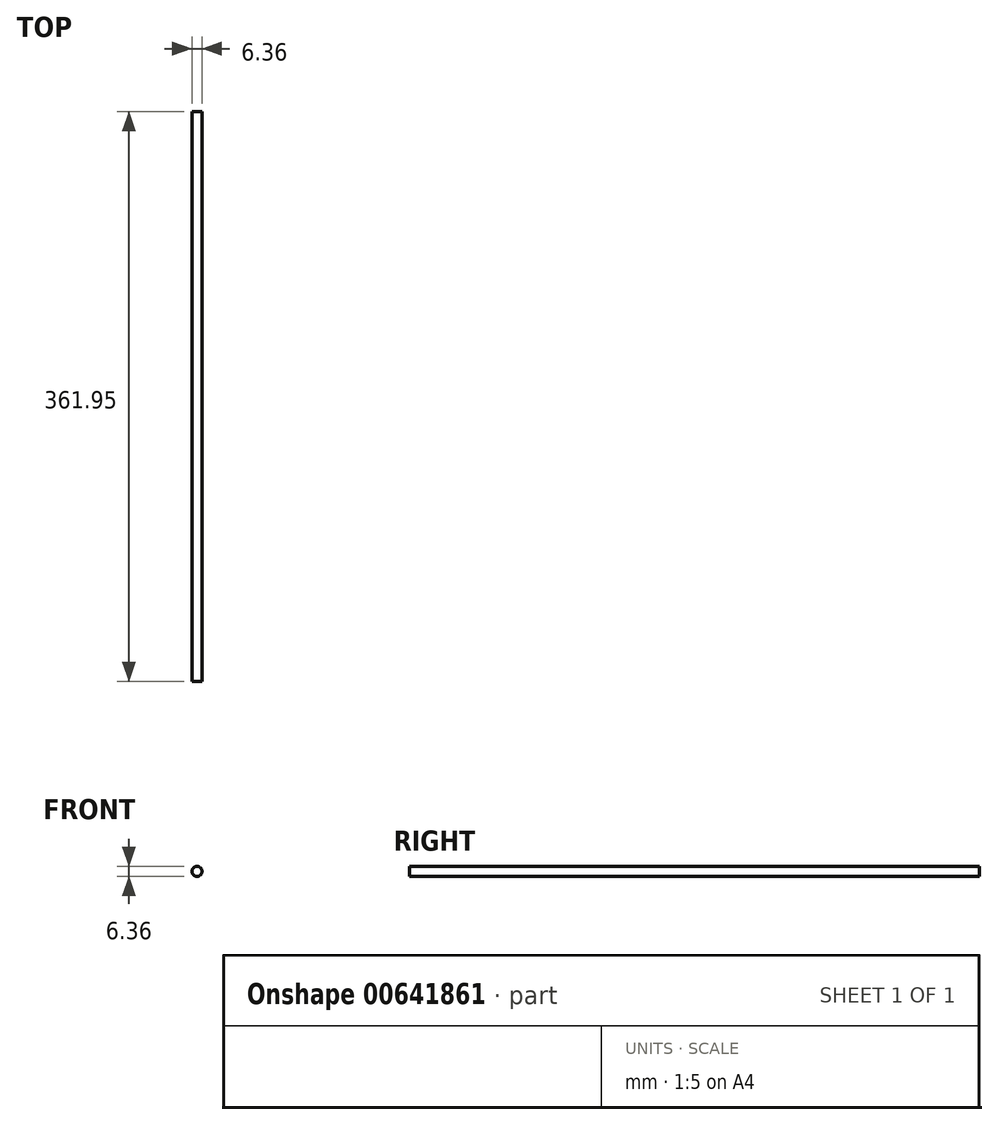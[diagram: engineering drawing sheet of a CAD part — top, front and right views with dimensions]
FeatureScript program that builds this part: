
annotation { "Feature Type Name" : "Feature", "Feature Type Description" : "" }
export const myFeature = defineFeature(function(context is Context, id is Id, definition is map)
    precondition{}
    {
        {
            var Q0;
            Q0=qCreatedBy(makeId("Front.planeOp"),FACE);
            var sketch = newSketch(context, id + "F0", { "sketchPlane" : qUnion([Q0])});
            skCircle(sketch, "E0", {"center": v(0, 0) * mm, "radius": 3.18 * mm});
            skSolve(sketch);
        }
        {
            var Q0;
            Q0 = qSketchRegion(id + "F0", true);
            extrude(context, id + "F1", {"entities" : qUnion([Q0]), "depth" : 361.95 * mm, "offsetDistance" : 25.4 * mm});
        }
    });
